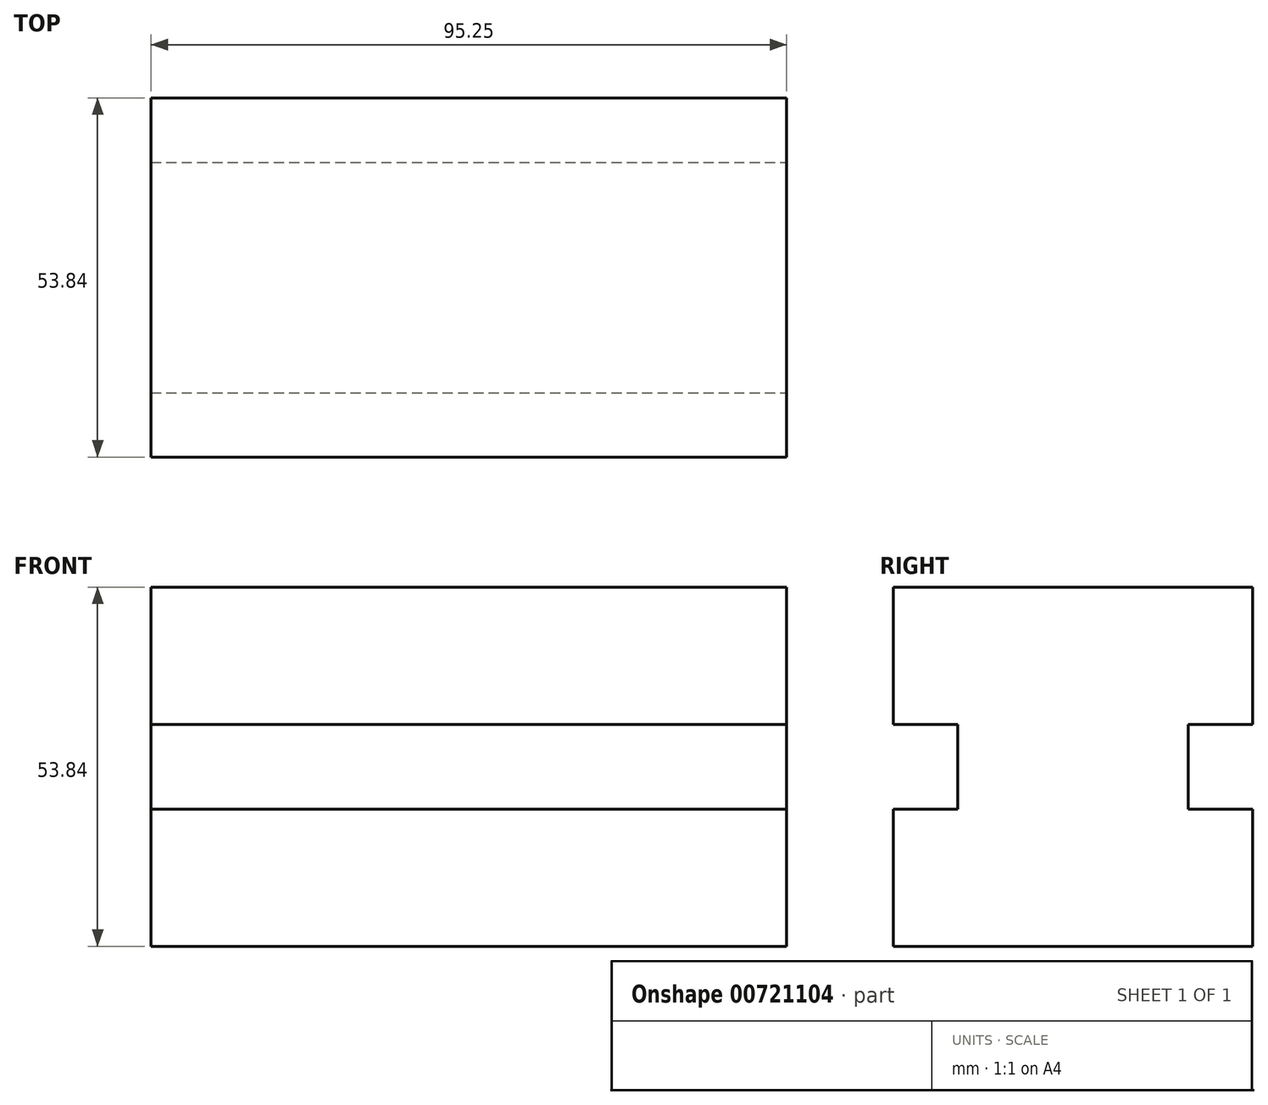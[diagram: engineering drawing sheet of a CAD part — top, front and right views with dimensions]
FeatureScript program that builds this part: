
annotation { "Feature Type Name" : "Feature", "Feature Type Description" : "" }
export const myFeature = defineFeature(function(context is Context, id is Id, definition is map)
    precondition{}
    {
        {
            var Q0;
            Q0=qCreatedBy(makeId("Right.planeOp"),FACE);
            var sketch = newSketch(context, id + "F0", { "sketchPlane" : qUnion([Q0])});
            skLineSegment(sketch, "E0.bottom", {"start": v(26.92, -26.92) * mm, "end": v(-26.92, -26.92) * mm});
            skLineSegment(sketch, "E0.top", {"start": v(26.92, 26.92) * mm, "end": v(-26.92, 26.92) * mm});
            skLineSegment(sketch, "E0.left", {"start": v(26.92, -26.92) * mm, "end": v(26.92, -6.35) * mm});
            skLineSegment(sketch, "E0.right", {"start": v(-26.92, -26.92) * mm, "end": v(-26.92, -6.35) * mm});
            skPoint(sketch, "E0.middle", {"position": v(0, 0) * mm});
            skLineSegment(sketch, "E1.bottom", {"start": v(-26.92, -6.35) * mm, "end": v(-17.27, -6.35) * mm});
            skLineSegment(sketch, "E1.top", {"start": v(-26.92, 6.35) * mm, "end": v(-17.27, 6.35) * mm});
            skLineSegment(sketch, "E1.right", {"start": v(-17.27, -6.35) * mm, "end": v(-17.27, 6.35) * mm});
            skLineSegment(sketch, "E2", {"start": v(0, 31.84) * mm, "end": v(0, -44.73) * mm, "construction": true});
            skLineSegment(sketch, "E3.MirrorCS", {"start": v(26.92, 6.35) * mm, "end": v(17.27, 6.35) * mm});
            skLineSegment(sketch, "E4.MirrorCS", {"start": v(17.27, -6.35) * mm, "end": v(17.27, 6.35) * mm});
            skLineSegment(sketch, "E5.MirrorCS", {"start": v(26.92, -6.35) * mm, "end": v(17.27, -6.35) * mm});
            skLineSegment(sketch, "E6.trimOffspring", {"start": v(-26.92, 6.35) * mm, "end": v(-26.92, 26.92) * mm});
            skLineSegment(sketch, "E7.trimOffspring", {"start": v(26.92, 6.35) * mm, "end": v(26.92, 26.92) * mm});
            skSolve(sketch);
        }
        {
            var Q0;
            Q0=makeQuery(id+"F0.imprint","IMPRINT",FACE,{"disambiguationData":[TD([[makeQuery(id+"F0.imprint","IMPRINT",EDGE,{"derivedFrom":sQuery(id+"F0.wireOp",EDGE,"E0.bottom")}),-1.0]])]});
            extrude(context, id + "F1", {"entities" : qUnion([Q0]), "oppositeDirection" : true, "depth" : 95.25 * mm, "offsetDistance" : 25.4 * mm});
        }
    });
